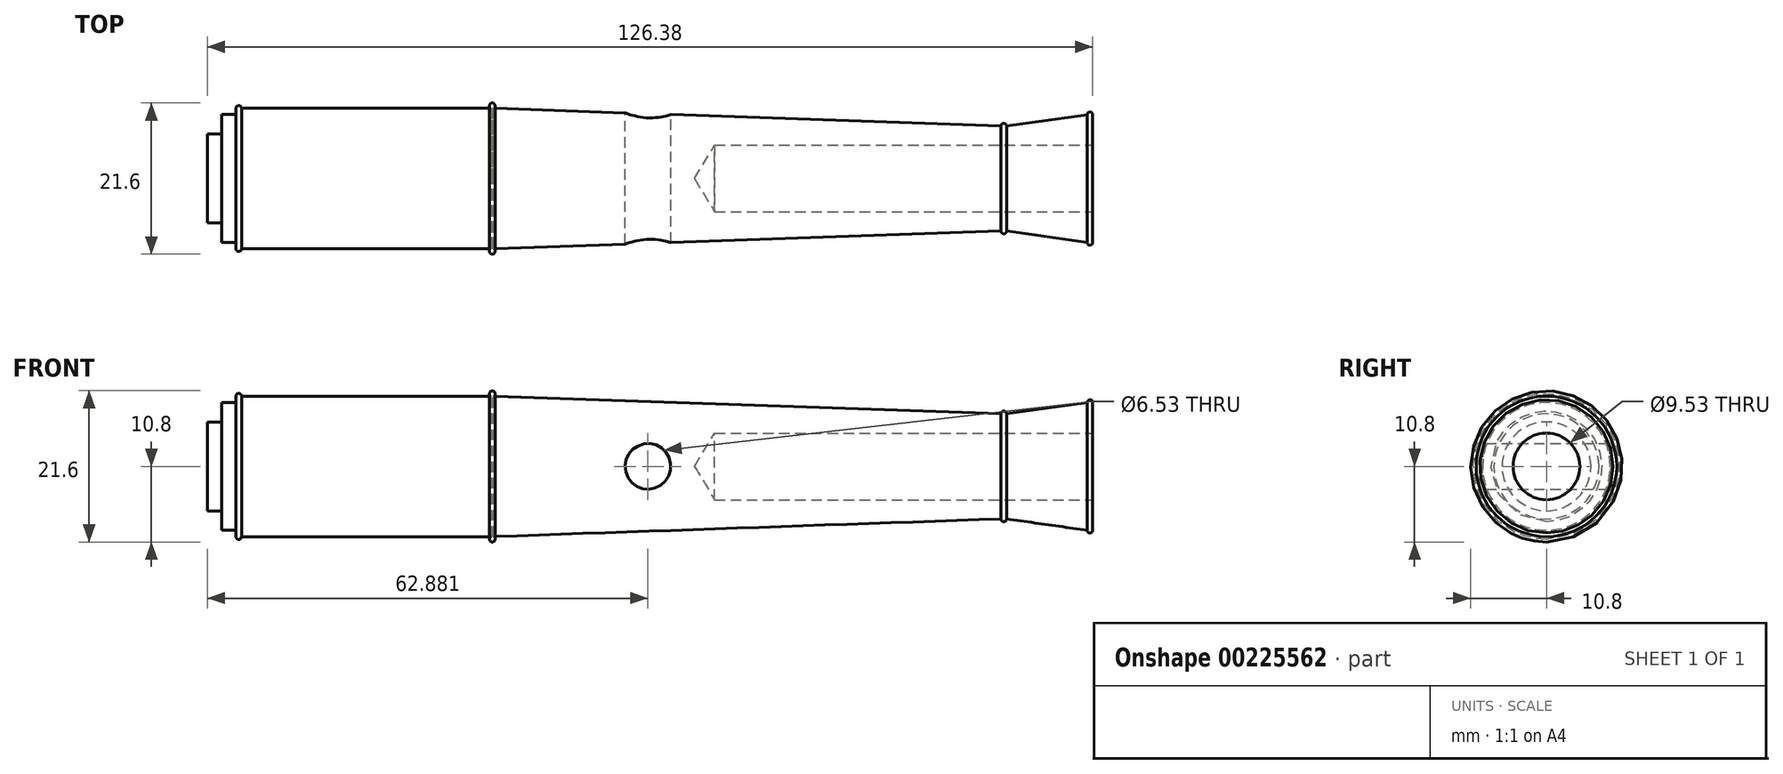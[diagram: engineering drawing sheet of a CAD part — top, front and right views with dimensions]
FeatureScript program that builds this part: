
annotation { "Feature Type Name" : "Feature", "Feature Type Description" : "" }
export const myFeature = defineFeature(function(context is Context, id is Id, definition is map)
    precondition{}
    {
        {
            var Q0;
            Q0=qCreatedBy(makeId("Front.planeOp"),FACE);
            var sketch = newSketch(context, id + "F0", { "sketchPlane" : qUnion([Q0])});
            skLineSegment(sketch, "E0", {"start": v(92.24, 0) * mm, "end": v(-34.14, 0) * mm});
            skLineSegment(sketch, "E1", {"start": v(-34.14, 0) * mm, "end": v(-34.14, 6.35) * mm});
            skLineSegment(sketch, "E2", {"start": v(-34.14, 6.35) * mm, "end": v(-32.1, 6.35) * mm});
            skLineSegment(sketch, "E3", {"start": v(-32.1, 6.35) * mm, "end": v(-32.1, 9.13) * mm});
            skLineSegment(sketch, "E4", {"start": v(-32.1, 9.13) * mm, "end": v(-30.07, 9.13) * mm});
            skLineSegment(sketch, "E5", {"start": v(-30.07, 9.13) * mm, "end": v(-30.07, 10.03) * mm});
            skLineSegment(sketch, "E6", {"start": v(-29.28, 10.03) * mm, "end": v(6.39, 10.03) * mm});
            skArc(sketch, "E7", {"start": v(-29.28, 10.03) * mm, "mid": v(-29.68, 10.43) * mm, "end": v(-30.07, 10.03) * mm});
            skArc(sketch, "E8", {"start": v(6.65, 10.03) * mm, "mid": v(6.52, 10.8) * mm, "end": v(6.39, 10.03) * mm});
            skLineSegment(sketch, "E9", {"start": v(6.65, 10.03) * mm, "end": v(79.15, 7.5) * mm});
            skLineSegment(sketch, "E10", {"start": v(6.65, 10.03) * mm, "end": v(22.03, 10.03) * mm, "construction": true});
            skArc(sketch, "E11", {"start": v(79.94, 7.5) * mm, "mid": v(79.54, 7.9) * mm, "end": v(79.15, 7.5) * mm});
            skLineSegment(sketch, "E12", {"start": v(79.94, 7.5) * mm, "end": v(91.45, 9.12) * mm});
            skArc(sketch, "E13", {"start": v(92.24, 9.12) * mm, "mid": v(91.85, 9.51) * mm, "end": v(91.45, 9.12) * mm});
            skLineSegment(sketch, "E14", {"start": v(91.45, 9.12) * mm, "end": v(87.5, 9.12) * mm, "construction": true});
            skLineSegment(sketch, "E15", {"start": v(92.24, 9.12) * mm, "end": v(92.24, 0) * mm});
            skSolve(sketch);
        }
        {
            var Q0;
            Q0 = qSketchRegion(id + "F0", true);
            var Q1;
            Q1=sQuery(id+"F0.wireOp",EDGE,"E0");
            revolve(context, id + "F1", {"entities" : qUnion([Q0]), "axis" : qUnion([Q1]), "revolveType" : RevolveType.FULL});
        }
        {
            var Q0;
            Q0=makeQuery(id+"F1.opRevolve","SWEPT_FACE",FACE,{"disambiguationData":[OSD([sQuery(id+"F0.wireOp",EDGE,"E15")])]});
            var sketch = newSketch(context, id + "F2", { "sketchPlane" : qUnion([Q0])});
            skPoint(sketch, "E16", {"position": v(0, 0) * mm});
            skSolve(sketch);
        }
        {
            var Q0;
            Q0=sQuery(id+"F2.wireOp",VERTEX,"E16");
            var Q1;
            Q1=makeQuery(id+"F1.opRevolve","SWEPT_BODY",BODY,{"disambiguationData":[OSD([sQuery(id+"F0.wireOp",EDGE,"E0"),sQuery(id+"F0.wireOp",EDGE,"E1"),sQuery(id+"F0.wireOp",EDGE,"E2"),sQuery(id+"F0.wireOp",EDGE,"E3"),sQuery(id+"F0.wireOp",EDGE,"E4"),sQuery(id+"F0.wireOp",EDGE,"E5"),sQuery(id+"F0.wireOp",EDGE,"E6"),sQuery(id+"F0.wireOp",EDGE,"E7"),sQuery(id+"F0.wireOp",EDGE,"E8"),sQuery(id+"F0.wireOp",EDGE,"E9"),sQuery(id+"F0.wireOp",EDGE,"E11"),sQuery(id+"F0.wireOp",EDGE,"E12"),sQuery(id+"F0.wireOp",EDGE,"E13"),sQuery(id+"F0.wireOp",EDGE,"E15")])]});
            hole(context, id + "F3", {"style" : HoleStyle.SIMPLE, "endStyle" : HoleEndStyle.BLIND, "holeDiameter" : 9.52 * mm, "holeDepth" : 53.97 * mm, "locations" : qUnion([Q0]), "scope" : qUnion([Q1])});
        }
        {
            var Q0;
            Q0=qCreatedBy(makeId("Front.planeOp"),FACE);
            var sketch = newSketch(context, id + "F4", { "sketchPlane" : qUnion([Q0])});
            skPoint(sketch, "E17", {"position": v(28.74, 0) * mm});
            skSolve(sketch);
        }
        {
            var Q0;
            Q0=sQuery(id+"F4.wireOp",VERTEX,"E17");
            var Q1;
            Q1=makeQuery(id+"F1.opRevolve","SWEPT_BODY",BODY,{"disambiguationData":[OSD([sQuery(id+"F0.wireOp",EDGE,"E0"),sQuery(id+"F0.wireOp",EDGE,"E1"),sQuery(id+"F0.wireOp",EDGE,"E2"),sQuery(id+"F0.wireOp",EDGE,"E3"),sQuery(id+"F0.wireOp",EDGE,"E4"),sQuery(id+"F0.wireOp",EDGE,"E5"),sQuery(id+"F0.wireOp",EDGE,"E6"),sQuery(id+"F0.wireOp",EDGE,"E7"),sQuery(id+"F0.wireOp",EDGE,"E8"),sQuery(id+"F0.wireOp",EDGE,"E9"),sQuery(id+"F0.wireOp",EDGE,"E11"),sQuery(id+"F0.wireOp",EDGE,"E12"),sQuery(id+"F0.wireOp",EDGE,"E13"),sQuery(id+"F0.wireOp",EDGE,"E15")])]});
            hole(context, id + "F5", {"style" : HoleStyle.SIMPLE, "endStyle" : HoleEndStyle.THROUGH, "oppositeDirection" : true, "holeDiameter" : 6.53 * mm, "locations" : qUnion([Q0]), "scope" : qUnion([Q1]), "isTappedThrough" : true});
        }
        {
            var Q0;
            Q0=qCreatedBy(makeId("Front.planeOp"),FACE);
            var sketch = newSketch(context, id + "F6", { "sketchPlane" : qUnion([Q0])});
            skPoint(sketch, "E18", {"position": v(28.74, 0) * mm});
            skSolve(sketch);
        }
        {
            var Q0;
            Q0=sQuery(id+"F6.wireOp",VERTEX,"E18");
            var Q1;
            Q1=makeQuery(id+"F1.opRevolve","SWEPT_BODY",BODY,{"disambiguationData":[OSD([sQuery(id+"F0.wireOp",EDGE,"E0"),sQuery(id+"F0.wireOp",EDGE,"E1"),sQuery(id+"F0.wireOp",EDGE,"E2"),sQuery(id+"F0.wireOp",EDGE,"E3"),sQuery(id+"F0.wireOp",EDGE,"E4"),sQuery(id+"F0.wireOp",EDGE,"E5"),sQuery(id+"F0.wireOp",EDGE,"E6"),sQuery(id+"F0.wireOp",EDGE,"E7"),sQuery(id+"F0.wireOp",EDGE,"E8"),sQuery(id+"F0.wireOp",EDGE,"E9"),sQuery(id+"F0.wireOp",EDGE,"E11"),sQuery(id+"F0.wireOp",EDGE,"E12"),sQuery(id+"F0.wireOp",EDGE,"E13"),sQuery(id+"F0.wireOp",EDGE,"E15")])]});
            hole(context, id + "F7", {"style" : HoleStyle.SIMPLE, "endStyle" : HoleEndStyle.THROUGH, "holeDiameter" : 6.53 * mm, "locations" : qUnion([Q0]), "scope" : qUnion([Q1]), "isTappedThrough" : true});
        }
    });
